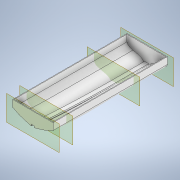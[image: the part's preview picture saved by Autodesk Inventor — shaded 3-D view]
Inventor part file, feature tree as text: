
AUTODESK INVENTOR PART (.ipt)
format: ipt  version: 2020.3 (Build 243373000, 373)  size: 314,880 bytes
history: native  units: mm
features: sketch x4, plane x4, loft x1, shell x1
ambient origin geometry x8: Origin, YZ Plane, XZ Plane, XY Plane, X Axis, Y Axis, Z Axis, Center Point
bodies: Solid1 (feature_tree)
feature tree (10):
  sketch  "Sketch1"  dims[d0=15.0mm d1=2.0mm d2=12.0mm]
  plane  "Work Plane4"
  loft  "Loft1"
  shell  "Shell1"  Thickness=12.0mm
  plane  "Work Plane1"
  plane  "Work Plane2"
  plane  "Work Plane3"
  sketch  "Sketch2"  dims[d3=24.0mm]
  sketch  "Sketch3"  dims[d4=9.0mm]
  sketch  "Sketch4"  dims[d5=6.0mm d6=24.0mm d7=6.0mm d8=12.0mm d9=9.0mm d10=60.0mm d11=10.0mm d12=-50.0mm d13=-100.0mm d14=-20.0mm d15=11.507923mm d16=2.0mm d17=6.0mm d18=6.0mm d19=9.0mm d20=9.0mm d21=12.0mm d22=12.0mm d23=24.0mm d24=24.0mm d25=10.0mm d26=2.0mm d29=0.0mm d30=90.0deg d31=0.0mm d32=90.0deg d35=10.0mm d36=90.0deg d37=0.0mm d38=90.0deg d40=5.0mm d41=20.0mm d42=20.0mm d43=5.0mm d44=1.0mm]
